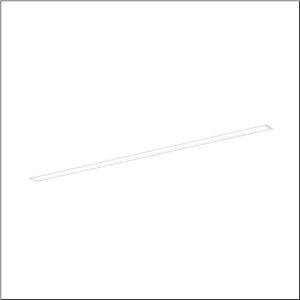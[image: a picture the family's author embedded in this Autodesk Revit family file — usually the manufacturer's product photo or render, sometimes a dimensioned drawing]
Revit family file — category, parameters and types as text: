
# Revit family: silica_r__21_51mx13db35wb_9931
name_source: partatom
category: Lighting Fixtures
units: mm (PartAtom-declared; Revit-internal decimal feet)

## family parameters
Cut with Voids When Loaded = No
Host = Face
Light Source = No
Part Type = Normal
Room Calculation Point = No
Round Connector Dimension = Use Diameter
Shared = No

## types (1)
- --- (1 x LED, 4100 lm, 30.1 W, 3000K)
    Apparent Load = 30 VA
    CIE Flux Codes = 78 96 99 100 100
    Color Rendering = 80
    Color Temperature = 3000K
    Default Elevation = 1800 mm
    Description = Silica® 21, office luminaire, primary optical cover: prismatic diffuser, of PMMA, CAT 2 (L<= 3000cd/m²), light emission: direct distribution, primary light characteristic: symmetric, installation type: recessed, LED, rated luminous flux: 4.100lm, luminous efficacy: 136lm/W, light colour: 830, colour temperature: 3000K, with terminal, 3+2-pole, max. 2.5mm², mains connection: 220..240V, AC, 50/60Hz, rated input power: 30.1W, luminaire housing, of aluminium, traffic white (RAL 9016), length: 1.528mm, width: 79mm, height: 53mm, protection rating (complete): IP20, insulation class (complete): insulation class I (protective earthing), certification: CE, permissible operating ambient temperature: 0..+35°C, standard: EN 50419, packaging unit: 1 piece
    Height = 0 mm  [stored 0 ft]
    Lamp = 1 x LED
    Lamp Light Flux = 4100 lm
    Lamp Power = 30.1 W
    Lamp count = 1
    Length = 1527 mm
    Luminous efficacy = 136 lm/W
    Manufacturer = Siteco
    ModVariant = No
    Model = 51MX13DB35WB
    Mounting Place = Ceiling
    Mounting Type = Recessed
    Number of Poles = 1
    OnlyDefault = Yes
    Power Factor = 1
    Product Name = Silica® 21
    Product group = office luminaire | ceiling recessed
    ProductGroupID = 401
    Protection Class = Protection class I
    Protection Degree = IP 20
    RLX_Detail_Level = 1
    RLX_Emergency_Light_Flux = 0 lm
    RLX_Emergency_Type = 0
    RLX_Emergency_Type_DB = No
    RlxData = <blob elided: 14241 chars, md5=68bb0056>
    Socket = socket
    Standby Power = 0 W
    System Light Flux = 4100 lm
    System Power = 30 W
    Type Comments = factory setting: luminous flux: 100 % | dim-lin: 254 | 345 mA
    Type Image = l_1251692.jpg
    URL = http://relux.com
    VarID = @adj_067561
    Voltage = 0 V
    Weight = 0.00 kg
    Width = 79 mm

note: [stored X ft] marks values corroborated as IEEE doubles in the binary element streams (Revit-internal decimal feet)

## geometry (parser evidence)
native form markers: Sweep x10
no freeform markers — native parametric forms only
